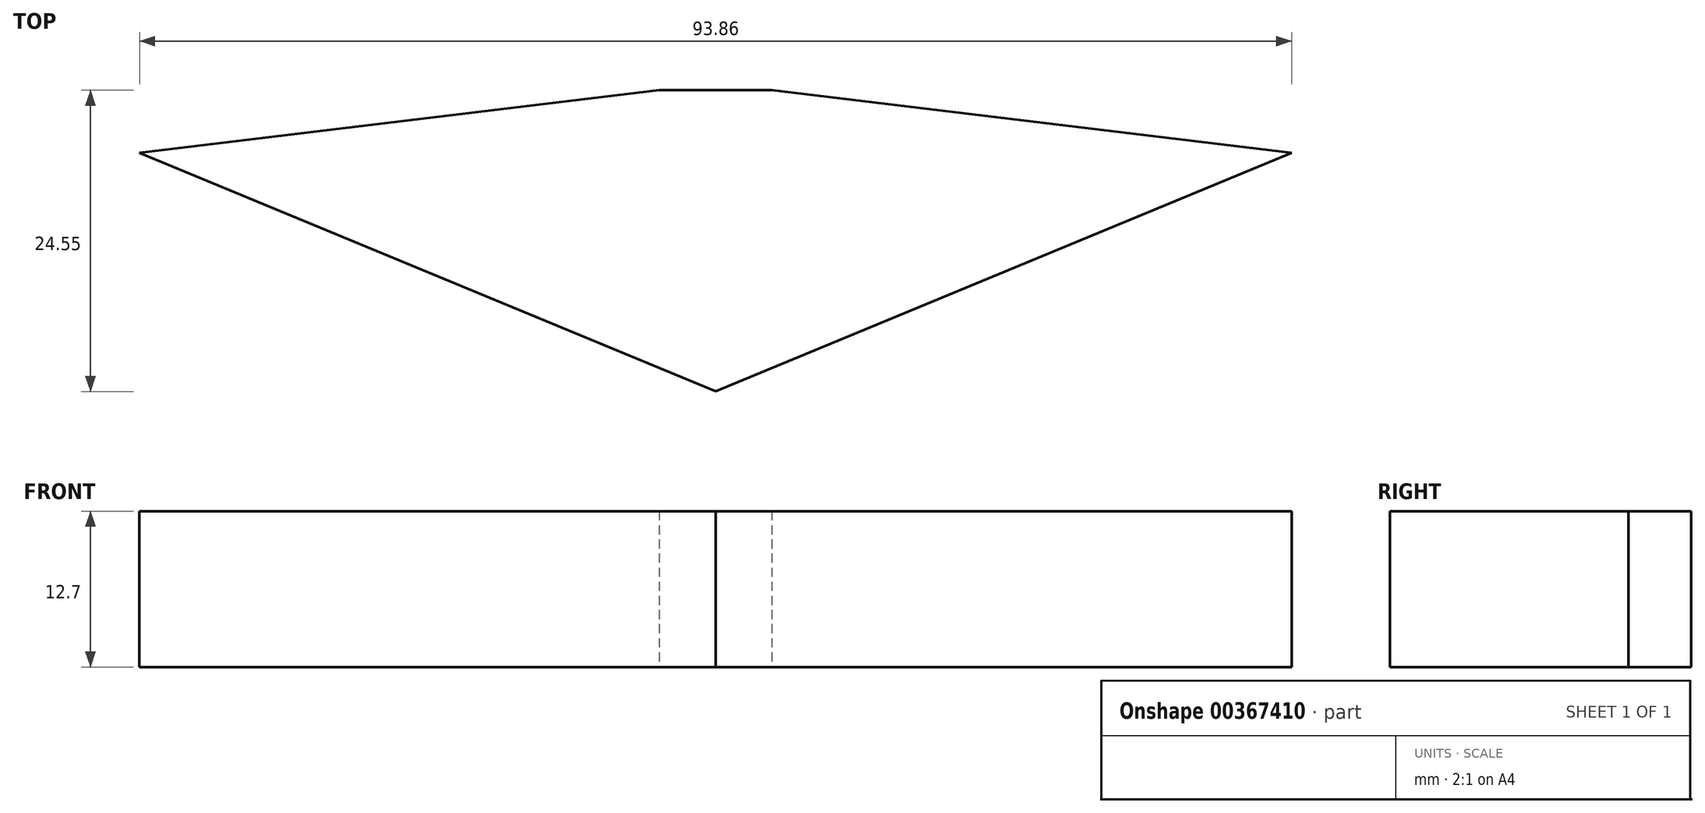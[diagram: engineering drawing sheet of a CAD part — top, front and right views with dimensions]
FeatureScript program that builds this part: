
annotation { "Feature Type Name" : "Feature", "Feature Type Description" : "" }
export const myFeature = defineFeature(function(context is Context, id is Id, definition is map)
    precondition{}
    {
        {
            var Q0;
            Q0=qCreatedBy(makeId("Top.planeOp"),FACE);
            var sketch = newSketch(context, id + "F0", { "sketchPlane" : qUnion([Q0])});
            skLineSegment(sketch, "E0", {"start": v(-46.93, -25.77) * mm, "end": v(0, -45.2) * mm});
            skLineSegment(sketch, "E1", {"start": v(0, -45.2) * mm, "end": v(46.93, -25.77) * mm});
            skLineSegment(sketch, "E2", {"start": v(46.93, -25.77) * mm, "end": v(0, 87.54) * mm});
            skLineSegment(sketch, "E3", {"start": v(0, 87.54) * mm, "end": v(-46.93, -25.77) * mm});
            skLineSegment(sketch, "E4", {"start": v(-4.6, -20.66) * mm, "end": v(4.6, -20.66) * mm});
            skLineSegment(sketch, "E5", {"start": v(4.6, -20.66) * mm, "end": v(0, 14.27) * mm});
            skLineSegment(sketch, "E6", {"start": v(0, 14.27) * mm, "end": v(-4.6, -20.66) * mm});
            skLineSegment(sketch, "E7", {"start": v(-46.93, -25.77) * mm, "end": v(-4.6, -20.66) * mm});
            skLineSegment(sketch, "E8", {"start": v(4.6, -20.66) * mm, "end": v(46.93, -25.77) * mm});
            skSolve(sketch);
        }
        {
            var Q0;
            Q0=makeQuery(id+"F0.imprint","IMPRINT",FACE,{"disambiguationData":[TD([[makeQuery(id+"F0.imprint","IMPRINT",EDGE,{"derivedFrom":sQuery(id+"F0.wireOp",EDGE,"E0")}),1.0]])]});
            extrude(context, id + "F1", {"entities" : qUnion([Q0]), "depth" : 12.7 * mm});
        }
    });
